# Revit family: 5864217284
name_source: partatom
category: Plumbing Fixtures
units: mm (PartAtom-declared; Revit-internal decimal feet)

## family parameters
Always vertical = Yes
Cut with Voids When Loaded = No
OmniClass Number = 23.45.55.00
OmniClass Title = Sanitary Faucets, Wastes
Part Type = Normal
Room Calculation Point = No
Round Connector Dimension = Use Diameter
Shared = No
Work Plane-Based = No

## types (1)
- 5864217284 Bath and shower faucet, 6 V, Bluetooth
    2D/3D/BIM Files URL = http://static.hansa.com
    3D View = https://static.hansa.com
    Additional Features = protected against back-flow in domestic use (according to DIN EN 1717)
    Advanced Features = Safety glass;Software settings adjustable via App
    Aerator = Standard aerator
    AssetType = Fixed
    BIMObjectName = 5864217284
    Backflow Prevention EN1717 = EB
    Battery = AA 1.5 V Lithium x 4
    Bluetooth = 4.x (D034445)
    BodyMaterial = Brass
    Brand = HANSA
    Catalog Drawing URL = http://static.hansa.com
    Category = Bathtub & Shower
    CloseOffRating = 0
    Color = Chrome/Grey
    Connection = Ball eccentric coupling(s)
    Connection Size = G1/2
    Default Elevation = 0 mm  [stored 0 ft]
    Dimension Drawing URL = http://static.hansa.com
    Diverter = Turn operated diverter;Integrated into flow control handle
    DurationUnit = Year
    EAN Number = 4057304008764
    EMC Directive = Radio Equipment Directive 2014/53/EU , 
Low Voltage Directive 2014/35/EU , 
EMC Directive 2014/30/EU , 
RoHS Directive 2011/65/EU
    EN Standard = EN 1111 , EN 15091, ETSI EN 301 489-1 V1.9.2 , 
ETSI EN 300 328 v2.2.2 , 
EN 61000-6-1:2007 , 
EN 61000-6-3:2007+A1:2011+AC:2012 , 
EN 60335-1:2012+A11+A13+A1+A14+A2+A15:2021, Part 19.11.4
    ETIM Class Number = EC010340 Electronic tap
    FDV Document URL = http://www.hansa.com
    FaucetMainMaterial = Brass
    Features = Thermostatic;Bluetooth®;Battery-operated
    Finish = Polished
    Flow Drawing URL = http://static.hansa.com
    Flow Rate At 300kPa = 0.3 L/s
    FlowCoefficient = 0
    Group = Bath and shower faucet
    IfcExportAs = IfcValveType
    IfcExportType = FAUCET
    Installation Type = Wall mounted
    Installation Width = CC150± 15 mm
    Installation and Maintenance Guide URL = http://static.hansa.com
    Interactive AR View URL = https://static.hansa.com
    Lever Handle = Temperature control handle;Flow control handle
    Manufacturer = HANSA
    ManufacturerName = HANSA
    ManufacturerURL = http://www.hansa.com
    Market = Austria;Belgium;Czech Republic;Germany;Spain;France;International;Italy;Netherlands;Slovakia
    Material = Brass
    Max. Hot Water Supply = 70 °C
    Mechanical Parts = Thermostatic cartridge for automatic temperature control
    Mobile Product Information URL = http://mpi.hansa.com
    Model = 5864217284 Bath and shower faucet, 6 V, Bluetooth
    ModelReference = 5864217284
    NBSDescription = Shower mixers
    NBSReference = 45-35-70/335
    Name = 5864217284 Bath and shower faucet, 6 V, Bluetooth
    Name_en = 5864217284 Bath and shower faucet, 6 V, Bluetooth
    Noise Class = I (ISO 3822) Oras lab.
    NominalDepth = 163 mm
    NominalHeight = 122 mm
    NominalWidth = 371 mm
    Operating Voltage = 6 V
    Pressure Loss With Flow 02ls = 300000.0 Pa
    Product Code = 5864217284
    Product Family = HANSAEMOTION Wellfit
    Product Image URL = http://static.hansa.com
    Product URL = http://static.hansa.com
    Protection Class = IP 55
    Sales Package dimensions (LxWxH) = 415 x 183 x 147
    Shape = Sculptured
    Size = 370x160x120 mm
    Spare-Part Information URL = http://static.hansa.com
    Spout Projection = 137 mm
    Surface treatment = Chrome/Grey
    Technical DataSheet URL = http://www.hansa.com
    Temperature = Thermostatic safety stop at 38°C;THERMO COOL
    Temperature Adjustments = Safety stop against scalding at 38°C;The housing of the fittings conducts minimal heat
    UNSPSC Class Number = 30181700 Faucets or taps
    URL Declaration Of Performance (DOP) = http://static.hansa.com
    URL Declaration of Asbestos = http://static.hansa.com
    URL Declaration of Conformity = http://static.hansa.com
    URL Declaration of SCIP = http://static.hansa.com
    URL EU Packaging Declaration = http://static.hansa.com
    URL EcoLabel Declaration = http://static.hansa.com
    URL REACH = http://static.hansa.com
    URL UN38.3 = http://static.hansa.com
    URL WEEE = http://static.hansa.com
    Uniclass2 = Pr_40_30_96_81
    Uniclass2015Description = Shower thermostatic water supply sets
    Uniclass2015Reference = Pr_40_20_87_81
    Version = 1
    VersionDate = 01/06/2023
    Warranty Information URL = http://warranty.hansa.com
    WarrantyDescription = http://warranty.hansa.com
    WarrantyDurationUnit = Year
    Working Pressure = 100 - 1000 kPa

note: [stored X ft] marks values corroborated as IEEE doubles in the binary element streams (Revit-internal decimal feet)

## geometry (parser evidence)
native form markers: Sweep x6
no freeform markers — native parametric forms only
